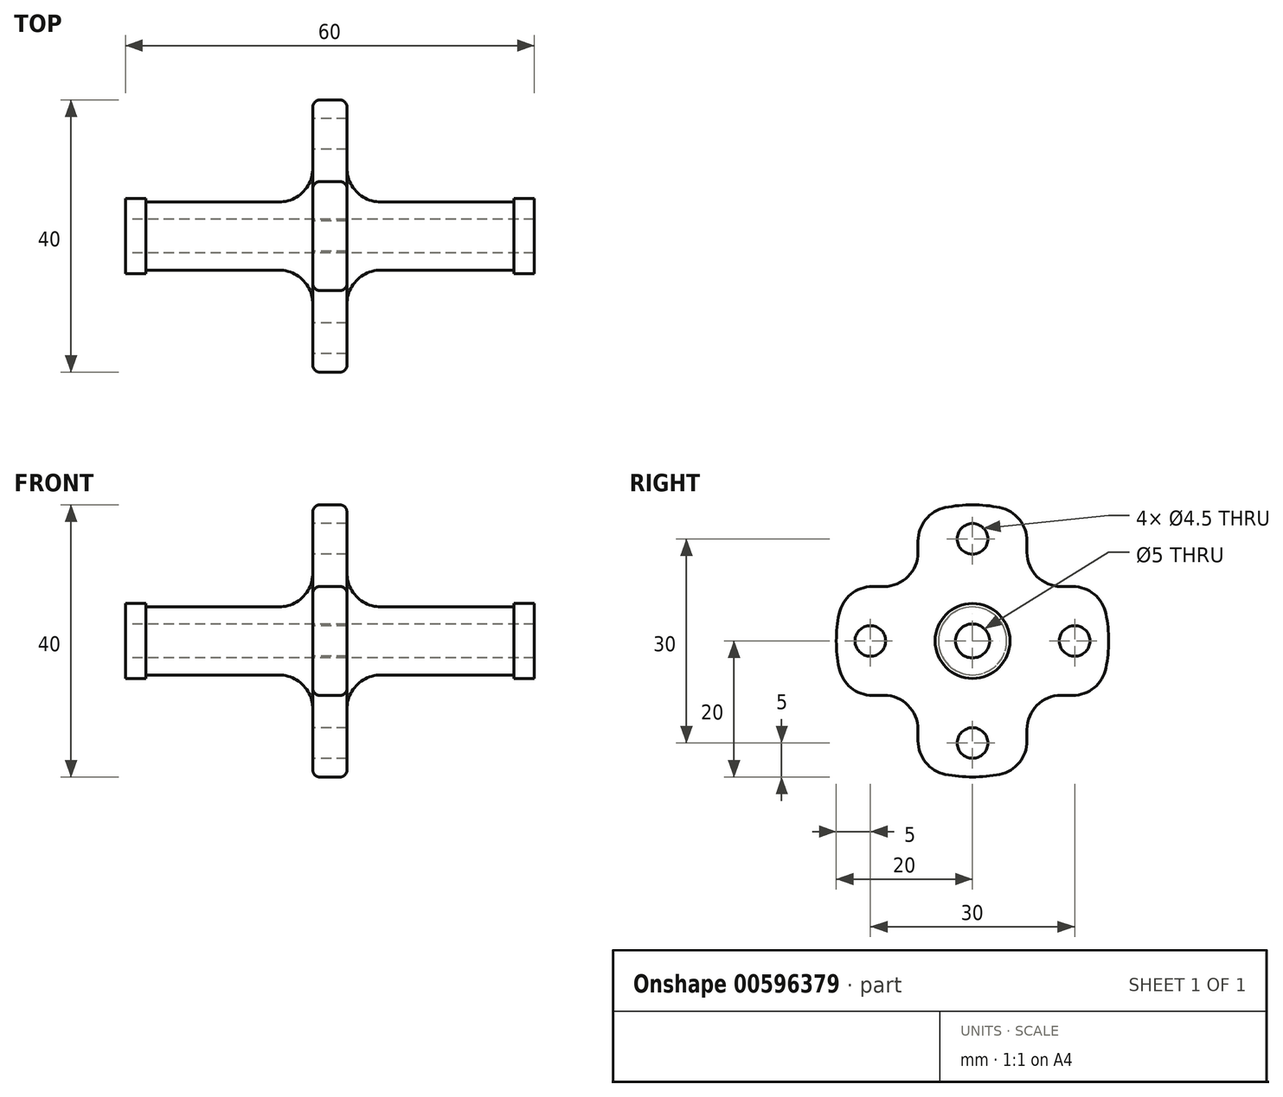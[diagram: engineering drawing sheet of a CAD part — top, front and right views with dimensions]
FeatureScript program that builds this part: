
annotation { "Feature Type Name" : "Feature", "Feature Type Description" : "" }
export const myFeature = defineFeature(function(context is Context, id is Id, definition is map)
    precondition{}
    {
        {
            var Q0;
            Q0=qCreatedBy(makeId("Front.planeOp"),FACE);
            var sketch = newSketch(context, id + "F0", { "sketchPlane" : qUnion([Q0])});
            skLineSegment(sketch, "E0", {"start": v(-30, 2.5) * mm, "end": v(30, 2.5) * mm});
            skLineSegment(sketch, "E1", {"start": v(-30, 2.5) * mm, "end": v(-30, 5.5) * mm});
            skLineSegment(sketch, "E2", {"start": v(-30, 5.5) * mm, "end": v(-27, 5.5) * mm});
            skLineSegment(sketch, "E3", {"start": v(-27, 5.5) * mm, "end": v(-27, 5) * mm});
            skLineSegment(sketch, "E4", {"start": v(-27, 5) * mm, "end": v(-2.5, 5) * mm});
            skLineSegment(sketch, "E5", {"start": v(-2.5, 5) * mm, "end": v(-2.5, 20) * mm});
            skLineSegment(sketch, "E6", {"start": v(-2.5, 20) * mm, "end": v(2.5, 20) * mm});
            skLineSegment(sketch, "E7", {"start": v(2.5, 20) * mm, "end": v(2.5, 5) * mm});
            skLineSegment(sketch, "E8", {"start": v(2.5, 5) * mm, "end": v(27, 5) * mm});
            skLineSegment(sketch, "E9", {"start": v(27, 5) * mm, "end": v(27, 5.5) * mm});
            skLineSegment(sketch, "E10", {"start": v(27, 5.5) * mm, "end": v(30, 5.5) * mm});
            skLineSegment(sketch, "E11", {"start": v(30, 5.5) * mm, "end": v(30, 2.5) * mm});
            skLineSegment(sketch, "E12", {"start": v(-50.14, 0) * mm, "end": v(58.14, 0) * mm, "construction": true});
            skSolve(sketch);
        }
        {
            var Q0;
            Q0 = qSketchRegion(id + "F0", true);
            var Q1;
            Q1=sQuery(id+"F0.wireOp",EDGE,"E12");
            revolve(context, id + "F1", {"entities" : qUnion([Q0]), "axis" : qUnion([Q1]), "revolveType" : RevolveType.FULL});
        }
        {
            var Q0;
            Q0=qCreatedBy(makeId("Right.planeOp"),FACE);
            var sketch = newSketch(context, id + "F2", { "sketchPlane" : qUnion([Q0])});
            skCircle(sketch, "E13", {"center": v(0, 15) * mm, "radius": 2.25 * mm});
            skCircle(sketch, "E14", {"center": v(0, -15) * mm, "radius": 2.25 * mm});
            skCircle(sketch, "E15", {"center": v(15, 0) * mm, "radius": 2.25 * mm});
            skCircle(sketch, "E16", {"center": v(-15, 0) * mm, "radius": 2.25 * mm});
            skLineSegment(sketch, "E17.bottom", {"start": v(-18.85, 18.85) * mm, "end": v(-8, 18.85) * mm});
            skLineSegment(sketch, "E17.top", {"start": v(-18.85, 8) * mm, "end": v(-8, 8) * mm});
            skLineSegment(sketch, "E17.left", {"start": v(-18.85, 18.85) * mm, "end": v(-18.85, 8) * mm});
            skLineSegment(sketch, "E17.right", {"start": v(-8, 18.85) * mm, "end": v(-8, 8) * mm});
            skLineSegment(sketch, "E18.bottom", {"start": v(-18.85, -8) * mm, "end": v(-8, -8) * mm});
            skLineSegment(sketch, "E18.top", {"start": v(-18.85, -18.85) * mm, "end": v(-8, -18.85) * mm});
            skLineSegment(sketch, "E18.left", {"start": v(-18.85, -8) * mm, "end": v(-18.85, -18.85) * mm});
            skLineSegment(sketch, "E18.right", {"start": v(-8, -8) * mm, "end": v(-8, -18.85) * mm});
            skLineSegment(sketch, "E19.bottom", {"start": v(8, -8) * mm, "end": v(18.85, -8) * mm});
            skLineSegment(sketch, "E19.top", {"start": v(8, -18.85) * mm, "end": v(18.85, -18.85) * mm});
            skLineSegment(sketch, "E19.left", {"start": v(8, -8) * mm, "end": v(8, -18.85) * mm});
            skLineSegment(sketch, "E19.right", {"start": v(18.85, -8) * mm, "end": v(18.85, -18.85) * mm});
            skLineSegment(sketch, "E20.bottom", {"start": v(8, 18.85) * mm, "end": v(18.85, 18.85) * mm});
            skLineSegment(sketch, "E20.top", {"start": v(8, 8) * mm, "end": v(18.85, 8) * mm});
            skLineSegment(sketch, "E20.left", {"start": v(8, 18.85) * mm, "end": v(8, 8) * mm});
            skLineSegment(sketch, "E20.right", {"start": v(18.85, 18.85) * mm, "end": v(18.85, 8) * mm});
            skSolve(sketch);
        }
        {
            var Q0;
            Q0 = qSketchRegion(id + "F2", true);
            extrude(context, id + "F3", {"entities" : qUnion([Q0]), "operationType" : NewBodyOperationType.REMOVE, "endBound" : BoundingType.SYMMETRIC, "depth" : 100 * mm, "offsetDistance" : 25 * mm});
        }
        {
            var Q0;
            Q0=makeQuery(id+"F3.boolean.opBoolean","COPY",EDGE,{"derivedFrom":makeQuery(id+"F3.opExtrude","SWEPT_EDGE",EDGE,{"disambiguationData":[OSD([sQuery(id+"F2.wireOp",EDGE,"E17.top"),sQuery(id+"F2.wireOp",EDGE,"E17.right")])]})});
            var Q1;
            Q1=makeQuery(id+"F3.boolean.opBoolean","INTERSECT",EDGE,{"derivedFrom":[makeQuery(id+"F1.opRevolve","SWEPT_FACE",FACE,{"disambiguationData":[OSD([sQuery(id+"F0.wireOp",EDGE,"E6")])]}),makeQuery(id+"F3.opExtrude","SWEPT_FACE",FACE,{"disambiguationData":[OSD([sQuery(id+"F2.wireOp",EDGE,"E17.top")])]})]});
            var Q2;
            Q2=makeQuery(id+"F3.boolean.opBoolean","INTERSECT",EDGE,{"derivedFrom":[makeQuery(id+"F1.opRevolve","SWEPT_FACE",FACE,{"disambiguationData":[OSD([sQuery(id+"F0.wireOp",EDGE,"E6")])]}),makeQuery(id+"F3.opExtrude","SWEPT_FACE",FACE,{"disambiguationData":[OSD([sQuery(id+"F2.wireOp",EDGE,"E17.right")])]})]});
            var Q3;
            Q3=makeQuery(id+"F3.boolean.opBoolean","INTERSECT",EDGE,{"derivedFrom":[makeQuery(id+"F1.opRevolve","SWEPT_FACE",FACE,{"disambiguationData":[OSD([sQuery(id+"F0.wireOp",EDGE,"E6")])]}),makeQuery(id+"F3.opExtrude","SWEPT_FACE",FACE,{"disambiguationData":[OSD([sQuery(id+"F2.wireOp",EDGE,"E18.bottom")])]})]});
            var Q4;
            Q4=makeQuery(id+"F3.boolean.opBoolean","INTERSECT",EDGE,{"derivedFrom":[makeQuery(id+"F1.opRevolve","SWEPT_FACE",FACE,{"disambiguationData":[OSD([sQuery(id+"F0.wireOp",EDGE,"E6")])]}),makeQuery(id+"F3.opExtrude","SWEPT_FACE",FACE,{"disambiguationData":[OSD([sQuery(id+"F2.wireOp",EDGE,"E18.right")])]})]});
            var Q5;
            Q5=makeQuery(id+"F3.boolean.opBoolean","COPY",EDGE,{"derivedFrom":makeQuery(id+"F3.opExtrude","SWEPT_EDGE",EDGE,{"disambiguationData":[OSD([sQuery(id+"F2.wireOp",EDGE,"E18.bottom"),sQuery(id+"F2.wireOp",EDGE,"E18.right")])]})});
            var Q6;
            Q6=makeQuery(id+"F3.boolean.opBoolean","COPY",EDGE,{"derivedFrom":makeQuery(id+"F3.opExtrude","SWEPT_EDGE",EDGE,{"disambiguationData":[OSD([sQuery(id+"F2.wireOp",EDGE,"E19.bottom"),sQuery(id+"F2.wireOp",EDGE,"E19.left")])]})});
            var Q7;
            Q7=makeQuery(id+"F3.boolean.opBoolean","INTERSECT",EDGE,{"derivedFrom":[makeQuery(id+"F1.opRevolve","SWEPT_FACE",FACE,{"disambiguationData":[OSD([sQuery(id+"F0.wireOp",EDGE,"E6")])]}),makeQuery(id+"F3.opExtrude","SWEPT_FACE",FACE,{"disambiguationData":[OSD([sQuery(id+"F2.wireOp",EDGE,"E19.left")])]})]});
            var Q8;
            Q8=makeQuery(id+"F3.boolean.opBoolean","INTERSECT",EDGE,{"derivedFrom":[makeQuery(id+"F1.opRevolve","SWEPT_FACE",FACE,{"disambiguationData":[OSD([sQuery(id+"F0.wireOp",EDGE,"E6")])]}),makeQuery(id+"F3.opExtrude","SWEPT_FACE",FACE,{"disambiguationData":[OSD([sQuery(id+"F2.wireOp",EDGE,"E19.bottom")])]})]});
            var Q9;
            Q9=makeQuery(id+"F3.boolean.opBoolean","COPY",EDGE,{"derivedFrom":makeQuery(id+"F3.opExtrude","SWEPT_EDGE",EDGE,{"disambiguationData":[OSD([sQuery(id+"F2.wireOp",EDGE,"E20.top"),sQuery(id+"F2.wireOp",EDGE,"E20.left")])]})});
            var Q10;
            Q10=makeQuery(id+"F3.boolean.opBoolean","INTERSECT",EDGE,{"derivedFrom":[makeQuery(id+"F1.opRevolve","SWEPT_FACE",FACE,{"disambiguationData":[OSD([sQuery(id+"F0.wireOp",EDGE,"E6")])]}),makeQuery(id+"F3.opExtrude","SWEPT_FACE",FACE,{"disambiguationData":[OSD([sQuery(id+"F2.wireOp",EDGE,"E20.top")])]})]});
            var Q11;
            Q11=makeQuery(id+"F3.boolean.opBoolean","INTERSECT",EDGE,{"derivedFrom":[makeQuery(id+"F1.opRevolve","SWEPT_FACE",FACE,{"disambiguationData":[OSD([sQuery(id+"F0.wireOp",EDGE,"E6")])]}),makeQuery(id+"F3.opExtrude","SWEPT_FACE",FACE,{"disambiguationData":[OSD([sQuery(id+"F2.wireOp",EDGE,"E20.left")])]})]});
            fillet(context, id + "F4", {"entities" : qUnion([Q0, Q1, Q2, Q3, Q4, Q5, Q6, Q7, Q8, Q9, Q10, Q11]), "radius" : 5 * mm, "tangentPropagation" : true, "allowEdgeOverflow" : false});
        }
        {
            var Q0;
            Q0=makeQuery(id+"F1.opRevolve","SWEPT_EDGE",EDGE,{"disambiguationData":[OSD([sQuery(id+"F0.wireOp",EDGE,"E7"),sQuery(id+"F0.wireOp",EDGE,"E8")])]});
            var Q1;
            Q1=makeQuery(id+"F1.opRevolve","SWEPT_EDGE",EDGE,{"disambiguationData":[OSD([sQuery(id+"F0.wireOp",EDGE,"E4"),sQuery(id+"F0.wireOp",EDGE,"E5")])]});
            fillet(context, id + "F5", {"entities" : qUnion([Q0, Q1]), "radius" : 5 * mm, "tangentPropagation" : true, "allowEdgeOverflow" : false});
        }
        {
            var Q0;
            {var subQ0=sQuery(id+"F0.wireOp",EDGE,"E5");var subQ1=sQuery(id+"F0.wireOp",EDGE,"E6");Q0=makeQuery(id+"F3.boolean.opBoolean","SPLIT",EDGE,{"disambiguationData":[TD([makeQuery(id+"F3.opExtrude","SWEPT_FACE",FACE,{"disambiguationData":[OSD([sQuery(id+"F2.wireOp",EDGE,"E17.top")])]})])],"derivedFrom":makeQuery(id+"F1.opRevolve","SWEPT_EDGE",EDGE,{"disambiguationData":[OSD([subQ0,subQ1])]})});}
            var Q1;
            {var subQ0=sQuery(id+"F0.wireOp",EDGE,"E6");var subQ1=sQuery(id+"F0.wireOp",EDGE,"E7");Q1=makeQuery(id+"F3.boolean.opBoolean","SPLIT",EDGE,{"disambiguationData":[TD([makeQuery(id+"F3.opExtrude","SWEPT_FACE",FACE,{"disambiguationData":[OSD([sQuery(id+"F2.wireOp",EDGE,"E17.top")])]})])],"derivedFrom":makeQuery(id+"F1.opRevolve","SWEPT_EDGE",EDGE,{"disambiguationData":[OSD([subQ0,subQ1])]})});}
            fillet(context, id + "F6", {"entities" : qUnion([Q0, Q1]), "radius" : 1 * mm, "tangentPropagation" : true, "allowEdgeOverflow" : false});
        }
    });
